# Revit family: QF_BOURGEAT_Transtherm_Four_sur_pietement_bas_5GN1_1_et_7GN1_1
name_source: partatom
category: Equipement spécialisé
revit_build: Autodesk Revit 2015 (Build: 20140606_1530(x64)
units: mm (PartAtom-declared; Revit-internal decimal feet)

## types (4) — shared parameters
Certification = NF alimentaire
Débit Eau Adoucie = 0.0 L/s
Fabricant = BOURGEAT
Fréquence = 50 Hz
Indice de protection = IP25
Longueur hors tout = 682 mm
Nature isolant = Laine_de_roche(60mm)
Phase = 3
Profondeur hors tout = 720 mm  [stored 2.3622 ft]
Remarques Plomberie = Débit=0.000083L/s
Spécification du Fabricant = TRANS'THERM
URL catalogue = http://www.bourgeat.fr

## per-type parameters (varying)
| type | Charge max | Consommation énergétique | Hauteur hors tout | Intensité nominale | Modèle | Poids net à vide | Puissance électrique  | Tension | Type_de_modele |
| 892205 + 895105 | 20.00 kg | 2.84Kwh/h | 845 mm  [stored 2.77231 ft] | 15 A | 892205 + 895105 | 48.00 kg | 3500 W | 230 V | 892205 + 895105 |
| 892205 + 895105 + 897500 | 20.00 kg | 2.84Kwh/h | 845 mm  [stored 2.77231 ft] | 15 A | 892205 + 897500 + 895105 | 48.00 kg | 3500 W | 230 V | 892205 + 897500 + 895105 |
| 892207 + 895105 | 28.00 kg | 4Kwh/h | 1004 mm  [stored 3.29396 ft] | 17 A | 892207 + 895105 | 55.00 kg | 6800 W | 400 V | 892207 + 895105 |
| 892207 + 897500 + 895105 | 28.00 kg | 4Kwh/h | 1004 mm  [stored 3.29396 ft] | 17 A | 892207 + 897500 + 895105 | 55.00 kg | 6800 W | 400 V | 892207 + 897500 + 895105 |

note: [stored X ft] marks values corroborated as IEEE doubles in the binary element streams (Revit-internal decimal feet)
